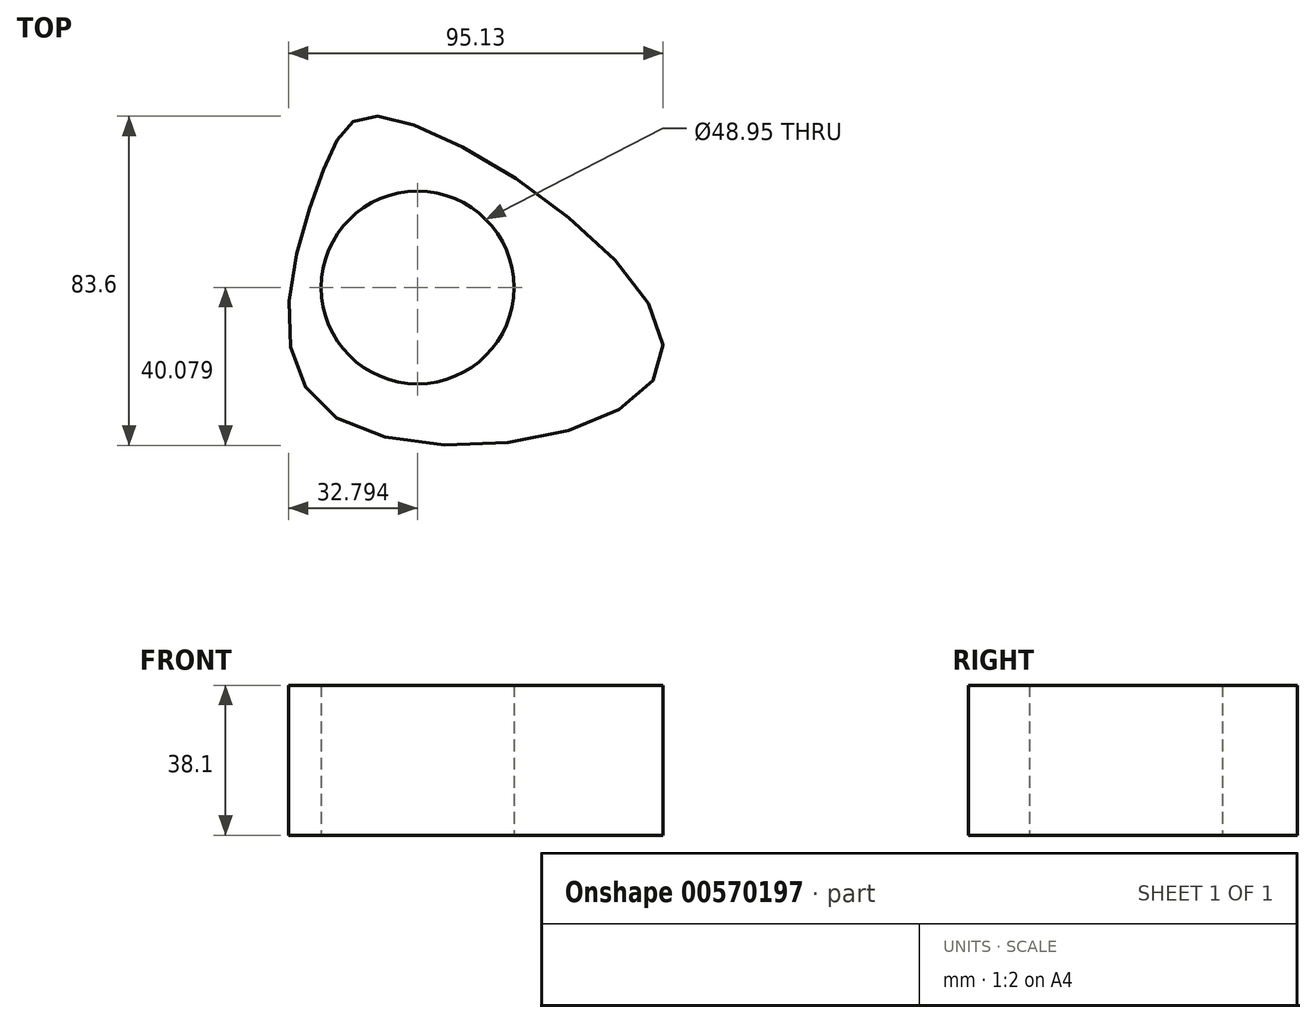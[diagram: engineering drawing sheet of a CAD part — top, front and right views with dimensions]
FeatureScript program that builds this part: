
annotation { "Feature Type Name" : "Feature", "Feature Type Description" : "" }
export const myFeature = defineFeature(function(context is Context, id is Id, definition is map)
    precondition{}
    {
        {
            var Q0;
            Q0=qCreatedBy(makeId("Top.planeOp"),FACE);
            var sketch = newSketch(context, id + "F0", { "sketchPlane" : qUnion([Q0])});
            skCircle(sketch, "E0", {"center": v(-4.95, 11.93) * mm, "radius": 24.47 * mm});
            skFitSpline(sketch, "E1", {"points": [v(-28.8, 41.9) * mm, v(-11.93, 54.99) * mm, v(57.03, -6.98) * mm, v(-27.93, -19.5) * mm, v(-28.8, 41.9) * mm]});
            skSolve(sketch);
        }
        {
            var Q0;
            Q0=makeQuery(id+"F0.imprint","IMPRINT",FACE,{"disambiguationData":[TD([[makeQuery(id+"F0.imprint","IMPRINT",EDGE,{"derivedFrom":sQuery(id+"F0.wireOp",EDGE,"E0")}),-1.0]])]});
            extrude(context, id + "F1", {"entities" : qUnion([Q0]), "depth" : 38.1 * mm, "offsetDistance" : 25.4 * mm});
        }
    });
